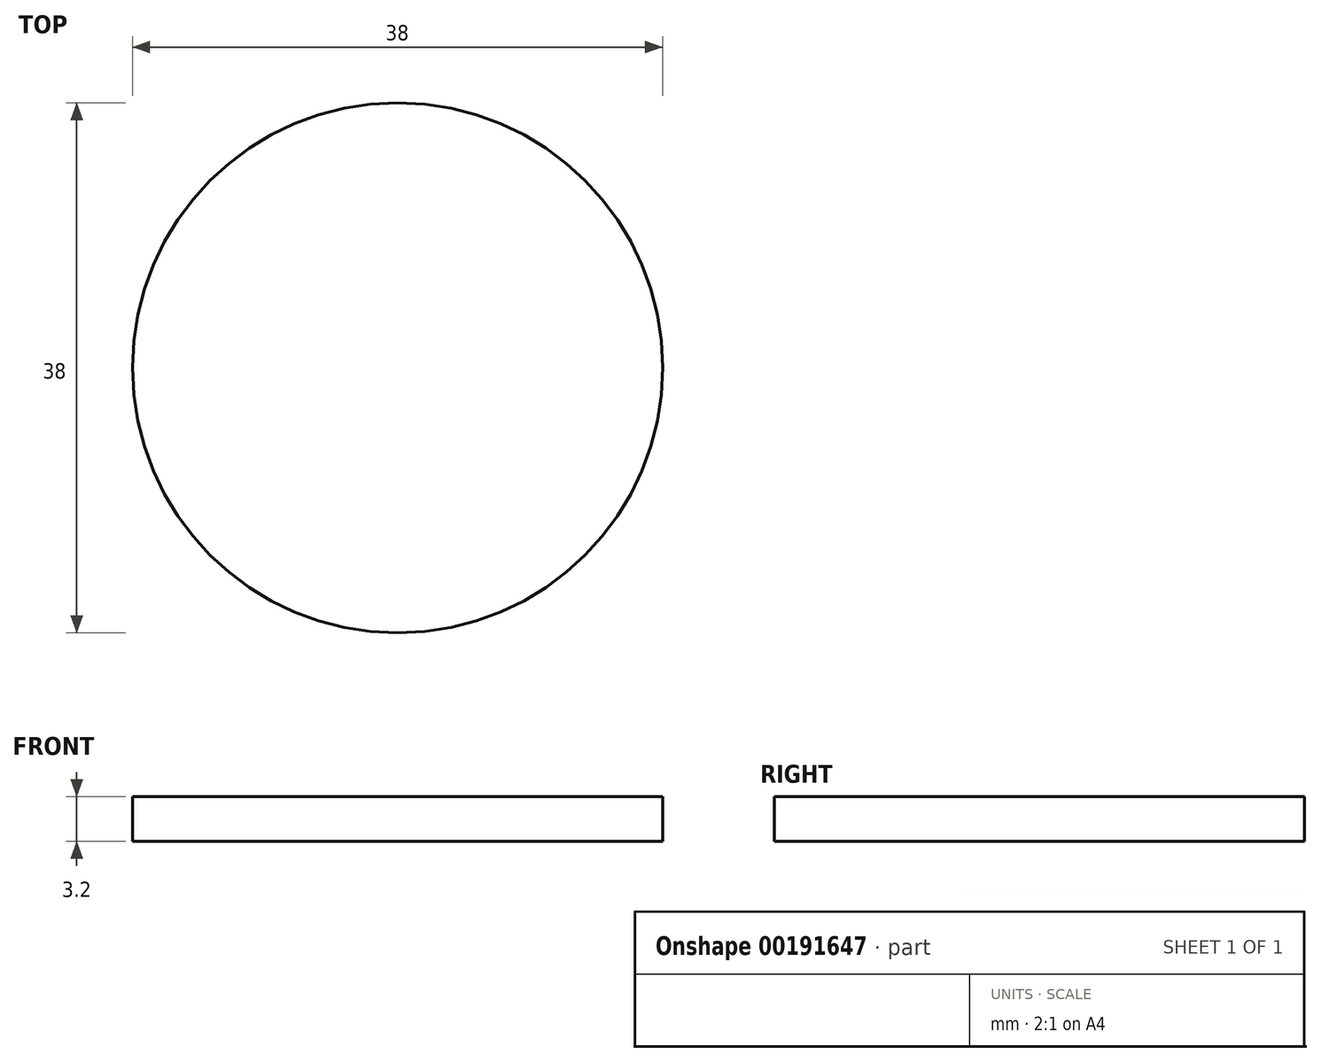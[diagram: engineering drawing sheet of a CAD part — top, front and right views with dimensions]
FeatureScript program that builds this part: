
annotation { "Feature Type Name" : "Feature", "Feature Type Description" : "" }
export const myFeature = defineFeature(function(context is Context, id is Id, definition is map)
    precondition{}
    {
        {
            var Q0;
            Q0=qCreatedBy(makeId("Top.planeOp"),FACE);
            var sketch = newSketch(context, id + "F0", { "sketchPlane" : qUnion([Q0])});
            skCircle(sketch, "E0", {"center": v(0, 0) * mm, "radius": 19 * mm});
            skSolve(sketch);
        }
        {
            var Q0;
            Q0 = qSketchRegion(id + "F0", true);
            extrude(context, id + "F1", {"entities" : qUnion([Q0]), "depth" : 3.2 * mm});
        }
    });
